# Revit family: 32L-CR-P-D
name_source: partatom
category: Lighting Fixtures
revit_build: Autodesk Revit 2014 (Build: 20130308_1515(x64)
units: mm (PartAtom-declared; Revit-internal decimal feet)

## types (3) — shared parameters
Apparent Load = 0 VA
Assembly Code = D5020210
Color Filter = 16777215
Default Elevation = 4' - 0"
Description = Inde-Pendant 32 LED Cylinder & Ring Pendant Direct
Dimming Lamp Color Temperature Shift = <None>
Emit Shape Visible in Rendering = No
Emit from Circle Diameter = 0' - 6"
Glass = Hubbell - Glass
Lamp = LED
Load Classification = Lighting
Manufacturer = Lite Control
Material = Hubbell Paint White
Pendant Height = 2' - 0"
Photometric Link = https://www.hubbell.com
Photometric Notes = More IES files downloaded in the Photometric Link
Photometric Web File = 32L-C-P-D-C1-AC1-30K-D055.IES
Power Factor = 1
Product Documentation Link = https://hubbellcdn.com
Product Page URL = https://www.hubbell.com
Tilt Angle = 90.00°
Type Comments = Lighting Fixtures
URL = https://www.hubbell.com
Voltage = 120 V
Warranty = 5 years Warranty
Watts = 7 W

## type names (no varying parameters)
- 32L-CR30-P-D
- 32L-CR20-P-D
- 32L-CR40-P-D

note: column(s) folded — value = type name in every type: Model, Ring Option

## geometry (parser evidence)
native form markers: Blend x1, Sweep x7
no freeform markers — native parametric forms only
